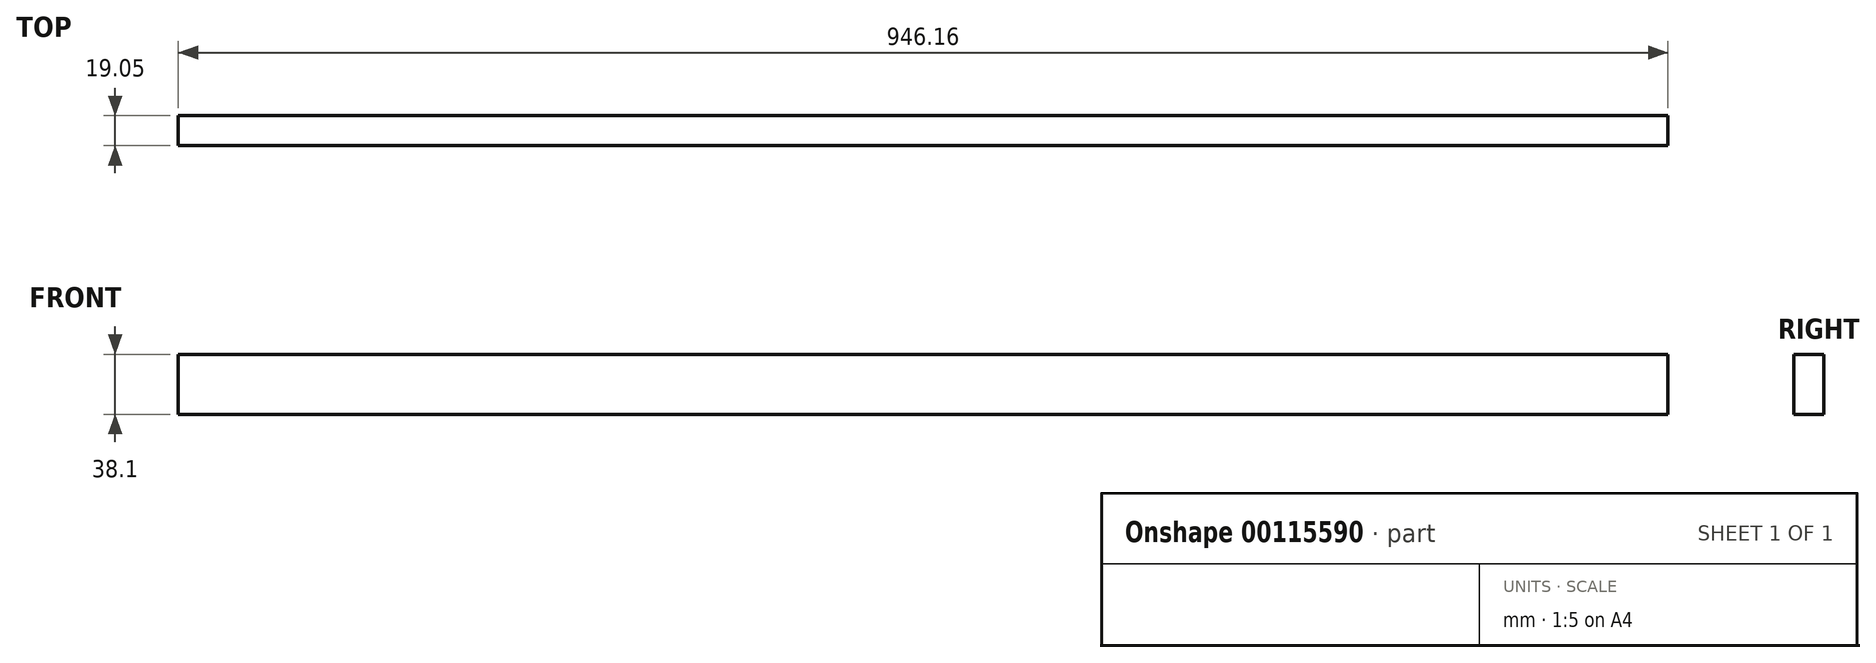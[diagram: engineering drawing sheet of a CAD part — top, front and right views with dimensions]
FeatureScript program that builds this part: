
annotation { "Feature Type Name" : "Feature", "Feature Type Description" : "" }
export const myFeature = defineFeature(function(context is Context, id is Id, definition is map)
    precondition{}
    {
        {
            var Q0;
            Q0=qCreatedBy(makeId("Front.planeOp"),FACE);
            var sketch = newSketch(context, id + "F0", { "sketchPlane" : qUnion([Q0])});
            skLineSegment(sketch, "E0.bottom", {"start": v(-473.08, 19.05) * mm, "end": v(473.08, 19.05) * mm});
            skLineSegment(sketch, "E0.top", {"start": v(-473.08, -19.05) * mm, "end": v(473.08, -19.05) * mm});
            skLineSegment(sketch, "E0.left", {"start": v(-473.08, 19.05) * mm, "end": v(-473.08, -19.05) * mm});
            skLineSegment(sketch, "E0.right", {"start": v(473.08, 19.05) * mm, "end": v(473.08, -19.05) * mm});
            skPoint(sketch, "E0.middle", {"position": v(0, 0) * mm});
            skSolve(sketch);
        }
        {
            var Q0;
            Q0=makeQuery(id+"F0.imprint","IMPRINT",FACE,{"disambiguationData":[TD([[makeQuery(id+"F0.imprint","IMPRINT",EDGE,{"derivedFrom":sQuery(id+"F0.wireOp",EDGE,"E0.bottom")}),-1.0]])]});
            extrude(context, id + "F1", {"entities" : qUnion([Q0]), "depth" : 19.05 * mm});
        }
    });
